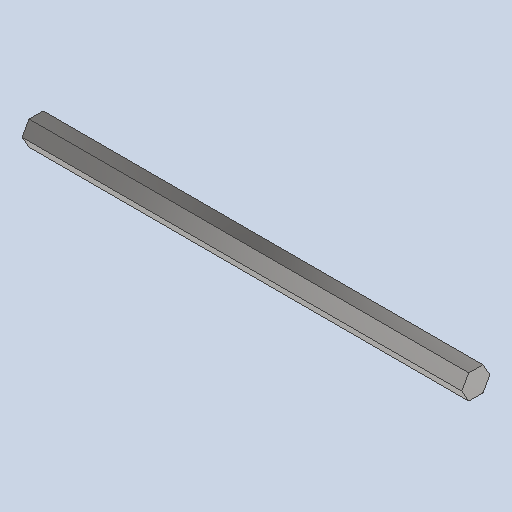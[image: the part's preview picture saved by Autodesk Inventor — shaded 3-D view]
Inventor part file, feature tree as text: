
AUTODESK INVENTOR PART (.ipt)
format: ipt  version: 2023 (Build 270158000, 158)  size: 91,648 bytes
history: native  units: in
note: dims shown in document units (in); Inventor stores cm internally (conversion verified against a paired STEP export)
features: other x3, sketch x1
ambient origin geometry x8: Origin, YZ Plane, XZ Plane, XY Plane, X Axis, Y Axis, Z Axis, Center Point
bodies: Solid1 (feature_tree)
feature tree (4):
  other  "9in-0.5inHexAxel_MIR1.ipt"
  other  "Solid1::9in-0.5inHexAxel_MIR1.ipt"
  other  "TaggingFeature1"
  sketch  "Sketch1"  dims[d0=0.3937in]
